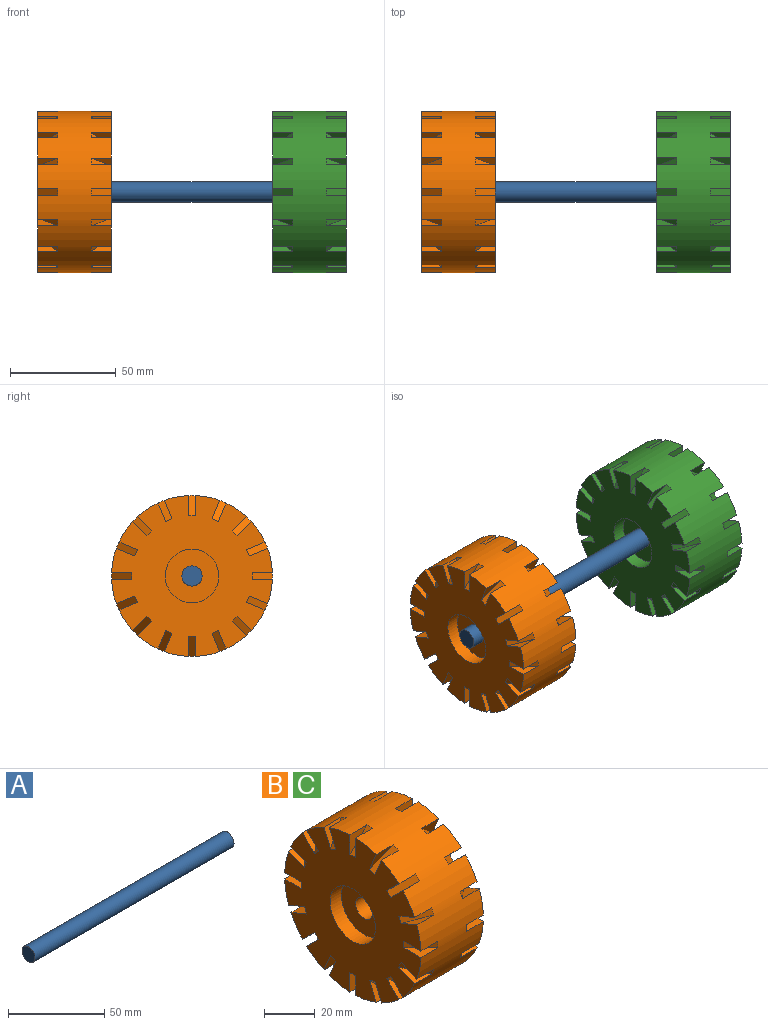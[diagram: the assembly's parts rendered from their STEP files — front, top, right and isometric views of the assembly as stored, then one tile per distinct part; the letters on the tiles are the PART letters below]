
ASSEMBLY  parts=3 mates=2
PART A: 3 faces, bbox 146.1x9.5x9.5 mm
  f0: cylinder r=4.76mm len=146.05mm, axis (-1,0,0), area 4370.4mm2, adj f1,f2
  f1: plane 9.53x9.53mm, normal (1,0,0), area 71.3mm2, adj f0
  f2: plane 9.53x9.53mm, normal (-1,0,0), area 71.3mm2, adj f0
PART B: 104 faces, bbox 34.9x76.2x76.2 mm
  f0: plane 76.13x76.13mm, normal (1,0,0), area 3570.4mm2, adj f1,f4,f5,f6,f7,f8,f9,f10
  f1: cylinder r=38.1mm len=76.2mm, axis (-1,0,0), area 7393.8mm2, adj f0,f5,f6,f7,f8,f9,f10,f11
  f2: cylinder r=4.76mm len=22.23mm, axis (-1,0,0), area 665.1mm2, adj f3,f54
  f3: plane 25.4x25.4mm, normal (1,0,0), area 435.5mm2, adj f2,f4
  f4: cylinder r=12.7mm len=25.4mm, axis (-1,0,0), area 506.7mm2, adj f0,f3
  f5: plane 9.53x9.53mm, normal (0.71,0,0.71), area 42.7mm2, adj f0,f1,f6,f7
  f6: plane 9.49x9.49mm, normal (0,1,0), area 45mm2, adj f0,f1,f5
  f7: plane 9.49x9.49mm, normal (0,-1,0), area 45mm2, adj f0,f1,f5
  f8: plane 9.98x9.53mm, normal (0.71,-0.27,0.65), area 42.7mm2, adj f0,f1,f9,f10
  f9: plane 9.49x8.77mm, normal (0,0.92,0.38), area 45mm2, adj f0,f1,f8
  f10: plane 9.49x8.77mm, normal (0,-0.92,-0.38), area 45mm2, adj f0,f1,f8
  f11: plane 9.53x8.96mm, normal (0.71,-0.5,0.5), area 42.7mm2, adj f0,f1,f12,f13
  f12: plane 9.49x6.71mm, normal (0,0.71,0.71), area 45mm2, adj f0,f1,f11
  f13: plane 9.49x6.71mm, normal (0,-0.71,-0.71), area 45mm2, adj f0,f1,f11
  f14: plane 9.98x9.53mm, normal (0.71,-0.65,0.27), area 42.7mm2, adj f0,f1,f15,f16
  f15: plane 9.49x8.77mm, normal (0,0.38,0.92), area 45mm2, adj f0,f1,f14
  f16: plane 9.49x8.77mm, normal (0,-0.38,-0.92), area 45mm2, adj f0,f1,f14
  f17: plane 9.53x9.53mm, normal (0.71,-0.71,0), area 42.7mm2, adj f0,f1,f18,f19
  f18: plane 9.49x9.49mm, normal (0,0,1), area 45mm2, adj f0,f1,f17
  f19: plane 9.49x9.49mm, normal (0,0,-1), area 45mm2, adj f0,f1,f17
  f20: plane 9.98x9.53mm, normal (0.71,-0.65,-0.27), area 42.7mm2, adj f0,f1,f21,f22
  f21: plane 9.49x8.77mm, normal (0,-0.38,0.92), area 45mm2, adj f0,f1,f20
  f22: plane 9.49x8.77mm, normal (0,0.38,-0.92), area 45mm2, adj f0,f1,f20
  f23: plane 9.53x8.96mm, normal (0.71,-0.5,-0.5), area 42.7mm2, adj f0,f1,f24,f25
  f24: plane 9.49x6.71mm, normal (0,-0.71,0.71), area 45mm2, adj f0,f1,f23
  f25: plane 9.49x6.71mm, normal (0,0.71,-0.71), area 45mm2, adj f0,f1,f23
  f26: plane 9.98x9.53mm, normal (0.71,-0.27,-0.65), area 42.7mm2, adj f0,f1,f27,f28
  f27: plane 9.49x8.77mm, normal (0,-0.92,0.38), area 45mm2, adj f0,f1,f26
  f28: plane 9.49x8.77mm, normal (0,0.92,-0.38), area 45mm2, adj f0,f1,f26
  f29: plane 9.53x9.53mm, normal (0.71,0,-0.71), area 42.7mm2, adj f0,f1,f30,f31
  f30: plane 9.49x9.49mm, normal (0,-1,0), area 45mm2, adj f0,f1,f29
  f31: plane 9.49x9.49mm, normal (0,1,0), area 45mm2, adj f0,f1,f29
  f32: plane 9.98x9.53mm, normal (0.71,0.27,-0.65), area 42.7mm2, adj f0,f1,f33,f34
  f33: plane 9.49x8.77mm, normal (0,-0.92,-0.38), area 45mm2, adj f0,f1,f32
  f34: plane 9.49x8.77mm, normal (0,0.92,0.38), area 45mm2, adj f0,f1,f32
  f35: plane 9.53x8.96mm, normal (0.71,0.5,-0.5), area 42.7mm2, adj f0,f1,f36,f37
  f36: plane 9.49x6.71mm, normal (0,-0.71,-0.71), area 45mm2, adj f0,f1,f35
  f37: plane 9.49x6.71mm, normal (0,0.71,0.71), area 45mm2, adj f0,f1,f35
  f38: plane 9.98x9.53mm, normal (0.71,0.65,-0.27), area 42.7mm2, adj f0,f1,f39,f40
  f39: plane 9.49x8.77mm, normal (0,-0.38,-0.92), area 45mm2, adj f0,f1,f38
  f40: plane 9.49x8.77mm, normal (0,0.38,0.92), area 45mm2, adj f0,f1,f38
  f41: plane 9.53x9.53mm, normal (0.71,0.71,0), area 42.7mm2, adj f0,f1,f42,f43
  f42: plane 9.49x9.49mm, normal (0,0,-1), area 45mm2, adj f0,f1,f41
  f43: plane 9.49x9.49mm, normal (0,0,1), area 45mm2, adj f0,f1,f41
  f44: plane 9.98x9.53mm, normal (0.71,0.65,0.27), area 42.7mm2, adj f0,f1,f45,f46
  f45: plane 9.49x8.77mm, normal (0,0.38,-0.92), area 45mm2, adj f0,f1,f44
  f46: plane 9.49x8.77mm, normal (0,-0.38,0.92), area 45mm2, adj f0,f1,f44
  f47: plane 9.53x8.96mm, normal (0.71,0.5,0.5), area 42.7mm2, adj f0,f1,f48,f49
  f48: plane 9.49x6.71mm, normal (0,0.71,-0.71), area 45mm2, adj f0,f1,f47
  f49: plane 9.49x6.71mm, normal (0,-0.71,0.71), area 45mm2, adj f0,f1,f47
  f50: plane 9.98x9.53mm, normal (0.71,0.27,0.65), area 42.7mm2, adj f0,f1,f51,f52
  f51: plane 9.49x8.77mm, normal (0,0.92,-0.38), area 45mm2, adj f0,f1,f50
  f52: plane 9.49x8.77mm, normal (0,-0.92,0.38), area 45mm2, adj f0,f1,f50
  f53: plane 76.13x76.13mm, normal (-1,0,0), area 3570.4mm2, adj f1,f55,f56,f57,f58,f59,f60,f61
  f54: plane 25.4x25.4mm, normal (-1,0,0), area 435.5mm2, adj f2,f55
  f55: cylinder r=12.7mm len=25.4mm, axis (1,0,0), area 506.7mm2, adj f53,f54
  f56: plane 9.53x9.53mm, normal (-0.71,0,0.71), area 42.7mm2, adj f1,f53,f57,f58
  f57: plane 9.49x9.49mm, normal (0,1,0), area 45mm2, adj f1,f53,f56
  f58: plane 9.49x9.49mm, normal (0,-1,0), area 45mm2, adj f1,f53,f56
  f59: plane 9.98x9.53mm, normal (-0.71,-0.27,0.65), area 42.7mm2, adj f1,f53,f60,f61
  f60: plane 9.49x8.77mm, normal (0,0.92,0.38), area 45mm2, adj f1,f53,f59
  f61: plane 9.49x8.77mm, normal (0,-0.92,-0.38), area 45mm2, adj f1,f53,f59
  f62: plane 9.53x8.96mm, normal (-0.71,-0.5,0.5), area 42.7mm2, adj f1,f53,f63,f64
  f63: plane 9.49x6.71mm, normal (0,0.71,0.71), area 45mm2, adj f1,f53,f62
  f64: plane 9.49x6.71mm, normal (0,-0.71,-0.71), area 45mm2, adj f1,f53,f62
  f65: plane 9.98x9.53mm, normal (-0.71,-0.65,0.27), area 42.7mm2, adj f1,f53,f66,f67
  f66: plane 9.49x8.77mm, normal (0,0.38,0.92), area 45mm2, adj f1,f53,f65
  f67: plane 9.49x8.77mm, normal (0,-0.38,-0.92), area 45mm2, adj f1,f53,f65
  f68: plane 9.53x9.53mm, normal (-0.71,-0.71,0), area 42.7mm2, adj f1,f53,f69,f70
  f69: plane 9.49x9.49mm, normal (0,0,1), area 45mm2, adj f1,f53,f68
  f70: plane 9.49x9.49mm, normal (0,0,-1), area 45mm2, adj f1,f53,f68
  f71: plane 9.98x9.53mm, normal (-0.71,-0.65,-0.27), area 42.7mm2, adj f1,f53,f72,f73
  f72: plane 9.49x8.77mm, normal (0,-0.38,0.92), area 45mm2, adj f1,f53,f71
  f73: plane 9.49x8.77mm, normal (0,0.38,-0.92), area 45mm2, adj f1,f53,f71
  f74: plane 9.53x8.96mm, normal (-0.71,-0.5,-0.5), area 42.7mm2, adj f1,f53,f75,f76
  f75: plane 9.49x6.71mm, normal (0,-0.71,0.71), area 45mm2, adj f1,f53,f74
  f76: plane 9.49x6.71mm, normal (0,0.71,-0.71), area 45mm2, adj f1,f53,f74
  f77: plane 9.98x9.53mm, normal (-0.71,-0.27,-0.65), area 42.7mm2, adj f1,f53,f78,f79
  f78: plane 9.49x8.77mm, normal (0,-0.92,0.38), area 45mm2, adj f1,f53,f77
  f79: plane 9.49x8.77mm, normal (0,0.92,-0.38), area 45mm2, adj f1,f53,f77
  f80: plane 9.53x9.53mm, normal (-0.71,0,-0.71), area 42.7mm2, adj f1,f53,f81,f82
  f81: plane 9.49x9.49mm, normal (0,-1,0), area 45mm2, adj f1,f53,f80
  f82: plane 9.49x9.49mm, normal (0,1,0), area 45mm2, adj f1,f53,f80
  f83: plane 9.98x9.53mm, normal (-0.71,0.27,-0.65), area 42.7mm2, adj f1,f53,f84,f85
  f84: plane 9.49x8.77mm, normal (0,-0.92,-0.38), area 45mm2, adj f1,f53,f83
  f85: plane 9.49x8.77mm, normal (0,0.92,0.38), area 45mm2, adj f1,f53,f83
  f86: plane 9.53x8.96mm, normal (-0.71,0.5,-0.5), area 42.7mm2, adj f1,f53,f87,f88
  f87: plane 9.49x6.71mm, normal (0,-0.71,-0.71), area 45mm2, adj f1,f53,f86
  f88: plane 9.49x6.71mm, normal (0,0.71,0.71), area 45mm2, adj f1,f53,f86
  f89: plane 9.98x9.53mm, normal (-0.71,0.65,-0.27), area 42.7mm2, adj f1,f53,f90,f91
  f90: plane 9.49x8.77mm, normal (0,-0.38,-0.92), area 45mm2, adj f1,f53,f89
  f91: plane 9.49x8.77mm, normal (0,0.38,0.92), area 45mm2, adj f1,f53,f89
  f92: plane 9.53x9.53mm, normal (-0.71,0.71,0), area 42.7mm2, adj f1,f53,f93,f94
  f93: plane 9.49x9.49mm, normal (0,0,-1), area 45mm2, adj f1,f53,f92
  f94: plane 9.49x9.49mm, normal (0,0,1), area 45mm2, adj f1,f53,f92
  f95: plane 9.98x9.53mm, normal (-0.71,0.65,0.27), area 42.7mm2, adj f1,f53,f96,f97
  f96: plane 9.49x8.77mm, normal (0,0.38,-0.92), area 45mm2, adj f1,f53,f95
  f97: plane 9.49x8.77mm, normal (0,-0.38,0.92), area 45mm2, adj f1,f53,f95
  f98: plane 9.53x8.96mm, normal (-0.71,0.5,0.5), area 42.7mm2, adj f1,f53,f99,f100
  f99: plane 9.49x6.71mm, normal (0,0.71,-0.71), area 45mm2, adj f1,f53,f98
  f100: plane 9.49x6.71mm, normal (0,-0.71,0.71), area 45mm2, adj f1,f53,f98
  f101: plane 9.98x9.53mm, normal (-0.71,0.27,0.65), area 42.7mm2, adj f1,f53,f102,f103
  f102: plane 9.49x8.77mm, normal (0,0.92,-0.38), area 45mm2, adj f1,f53,f101
  f103: plane 9.49x8.77mm, normal (0,-0.92,0.38), area 45mm2, adj f1,f53,f101
PART C: same geometry as B
PLACE A t=(0,-17.46,-7.94)mm fixed
PLACE B t=(-111.13,-17.46,-7.94)mm
PLACE C t=(0,-17.46,-7.94)mm
MATE fastened B.f1 <-> A.f0  axis (-1,0,0) through (-73.03,0,0)mm
MATE fastened C.f1 <-> A.f0  axis (-1,0,0) through (73.03,0,0)mm
